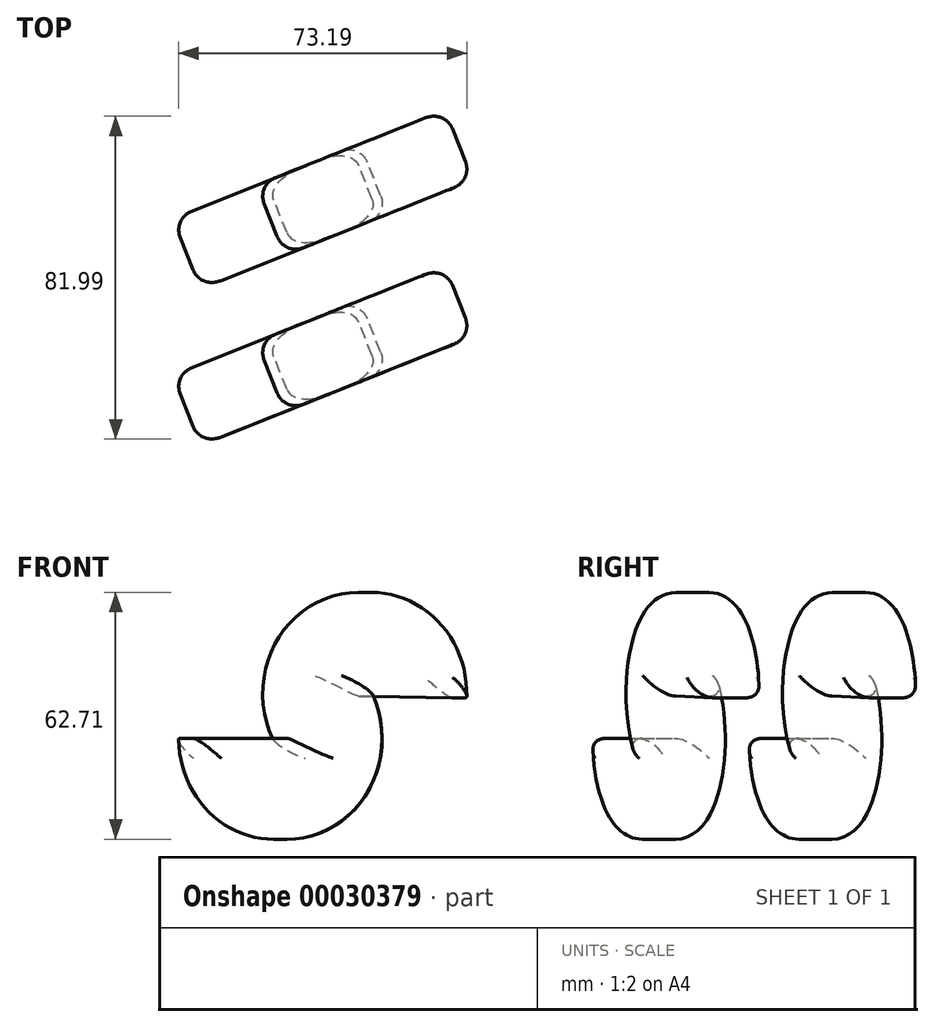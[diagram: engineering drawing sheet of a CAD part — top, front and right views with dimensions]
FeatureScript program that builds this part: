
annotation { "Feature Type Name" : "Feature", "Feature Type Description" : "" }
export const myFeature = defineFeature(function(context is Context, id is Id, definition is map)
    precondition{}
    {
        {
            var Q0;
            Q0=qCreatedBy(makeId("Top.planeOp"),FACE);
            var sketch = newSketch(context, id + "F0", { "sketchPlane" : qUnion([Q0])});
            skArc(sketch, "E0", {"start": v(-65.29, -37.17) * mm, "mid": v(-27.1, -48.9) * mm, "end": v(-23.84, -9.09) * mm});
            skArc(sketch, "E1", {"start": v(0, 0) * mm, "mid": v(-38.53, 12.83) * mm, "end": v(-41.48, -27.68) * mm});
            skLineSegment(sketch, "E2", {"start": v(-65.29, -37.17) * mm, "end": v(-41.48, -27.68) * mm});
            skLineSegment(sketch, "E3", {"start": v(-23.84, -9.09) * mm, "end": v(0, 0) * mm});
            skSolve(sketch);
        }
        {
            var Q0;
            Q0 = qSketchRegion(id + "F0", true);
            extrude(context, id + "F1", {"entities" : qUnion([Q0]), "depth" : 19.17 * mm});
        }
        {
            var Q0;
            Q0=makeQuery(id+"F1.opExtrude","CAP_EDGE",EDGE,{"disambiguationData":[OSD([sQuery(id+"F0.wireOp",EDGE,"E0")])],"isStart":false});
            var Q1;
            Q1=makeQuery(id+"F1.opExtrude","CAP_EDGE",EDGE,{"disambiguationData":[OSD([sQuery(id+"F0.wireOp",EDGE,"E3")])],"isStart":false});
            var Q2;
            Q2=makeQuery(id+"F1.opExtrude","CAP_EDGE",EDGE,{"disambiguationData":[OSD([sQuery(id+"F0.wireOp",EDGE,"E1")])],"isStart":false});
            var Q3;
            Q3=makeQuery(id+"F1.opExtrude","CAP_EDGE",EDGE,{"disambiguationData":[OSD([sQuery(id+"F0.wireOp",EDGE,"E2")])],"isStart":false});
            fillet(context, id + "F2", {"entities" : qUnion([Q0, Q1, Q2, Q3]), "radius" : 5.08 * mm, "tangentPropagation" : true, "allowEdgeOverflow" : false});
        }
        {
            var Q0;
            Q0=makeQuery(id+"F1.opExtrude","CAP_EDGE",EDGE,{"disambiguationData":[OSD([sQuery(id+"F0.wireOp",EDGE,"E1")])],"isStart":true});
            var Q1;
            Q1=makeQuery(id+"F1.opExtrude","CAP_EDGE",EDGE,{"disambiguationData":[OSD([sQuery(id+"F0.wireOp",EDGE,"E2")])],"isStart":true});
            var Q2;
            Q2=makeQuery(id+"F1.opExtrude","CAP_EDGE",EDGE,{"disambiguationData":[OSD([sQuery(id+"F0.wireOp",EDGE,"E0")])],"isStart":true});
            var Q3;
            Q3=makeQuery(id+"F1.opExtrude","CAP_EDGE",EDGE,{"disambiguationData":[OSD([sQuery(id+"F0.wireOp",EDGE,"E3")])],"isStart":true});
            fillet(context, id + "F3", {"entities" : qUnion([Q0, Q1, Q2, Q3]), "radius" : 5.08 * mm, "tangentPropagation" : true, "allowEdgeOverflow" : false});
        }
        {
            var Q0;
            Q0=makeQuery(id+"F1.opExtrude","SWEPT_BODY",BODY,{"disambiguationData":[OSD([sQuery(id+"F0.wireOp",EDGE,"E0"),sQuery(id+"F0.wireOp",EDGE,"E1"),sQuery(id+"F0.wireOp",EDGE,"E2"),sQuery(id+"F0.wireOp",EDGE,"E3")])]});
            var Q1;
            {var subQ0=sQuery(id+"F0.wireOp",EDGE,"E2");Q1=makeQuery(id+"F2.opFillet","BLEND_EDGE",EDGE,{"blendedFrom":[makeQuery(id+"F1.opExtrude","CAP_EDGE",EDGE,{"disambiguationData":[OSD([subQ0])],"isStart":false}),makeQuery(id+"F1.opExtrude","SWEPT_FACE",FACE,{"disambiguationData":[OSD([subQ0])]})],"blendedInto":[makeQuery(id+"F1.opExtrude","SWEPT_FACE",FACE,{"disambiguationData":[OSD([subQ0])]})]});}
            transform(context, id + "F4", {"entities" : qUnion([Q0]), "transformType" : TransformType.ROTATION, "transformAxis" : qUnion([Q1]), "angle" : 90 * degree, "makeCopy" : false});
        }
        {
            var Q0;
            Q0=makeQuery(id+"F1.opExtrude","SWEPT_BODY",BODY,{"disambiguationData":[OSD([sQuery(id+"F0.wireOp",EDGE,"E0"),sQuery(id+"F0.wireOp",EDGE,"E1"),sQuery(id+"F0.wireOp",EDGE,"E2"),sQuery(id+"F0.wireOp",EDGE,"E3")])]});
            var Q1;
            Q1=qCreatedBy(makeId("Top.planeOp"),FACE);
            transform(context, id + "F5", {"entities" : qUnion([Q0]), "transformType" : TransformType.TRANSLATION_DISTANCE, "transformDirection" : qUnion([Q1]), "distance" : 0.2 * mm, "oppositeDirection" : true, "makeCopy" : false});
        }
        {
            var Q0;
            Q0=makeQuery(id+"F1.opExtrude","SWEPT_BODY",BODY,{"disambiguationData":[OSD([sQuery(id+"F0.wireOp",EDGE,"E0"),sQuery(id+"F0.wireOp",EDGE,"E1"),sQuery(id+"F0.wireOp",EDGE,"E2"),sQuery(id+"F0.wireOp",EDGE,"E3")])]});
            var Q1;
            Q1=qCreatedBy(makeId("Front.planeOp"),FACE);
            transform(context, id + "F6", {"entities" : qUnion([Q0]), "transformType" : TransformType.TRANSLATION_DISTANCE, "transformDirection" : qUnion([Q1]), "distance" : 39.77 * mm, "makeCopy" : true});
        }
    });
